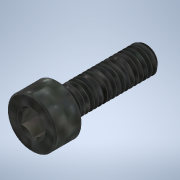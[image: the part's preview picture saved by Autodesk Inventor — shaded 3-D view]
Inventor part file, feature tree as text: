
AUTODESK INVENTOR PART (.ipt)
format: ipt  version: 2020.5 (Build 245400000, 400)  size: 612,352 bytes
history: native  units: in
note: dims shown in document units (in); Inventor stores cm internally (conversion verified against a paired STEP export)
features: revolve x1
ambient origin geometry x8: Origin, YZ Plane, XZ Plane, XY Plane, X Axis, Y Axis, Z Axis, Center Point
bodies: Solid1 (feature_tree)
feature tree (1):
  revolve  "Revolve2"  [1 undecoded]
note: 1 required parameter value undecoded (feature->parameter linkage not recoverable at this tier; creation-order binding heuristic only, values carry confidence <= 0.55)
